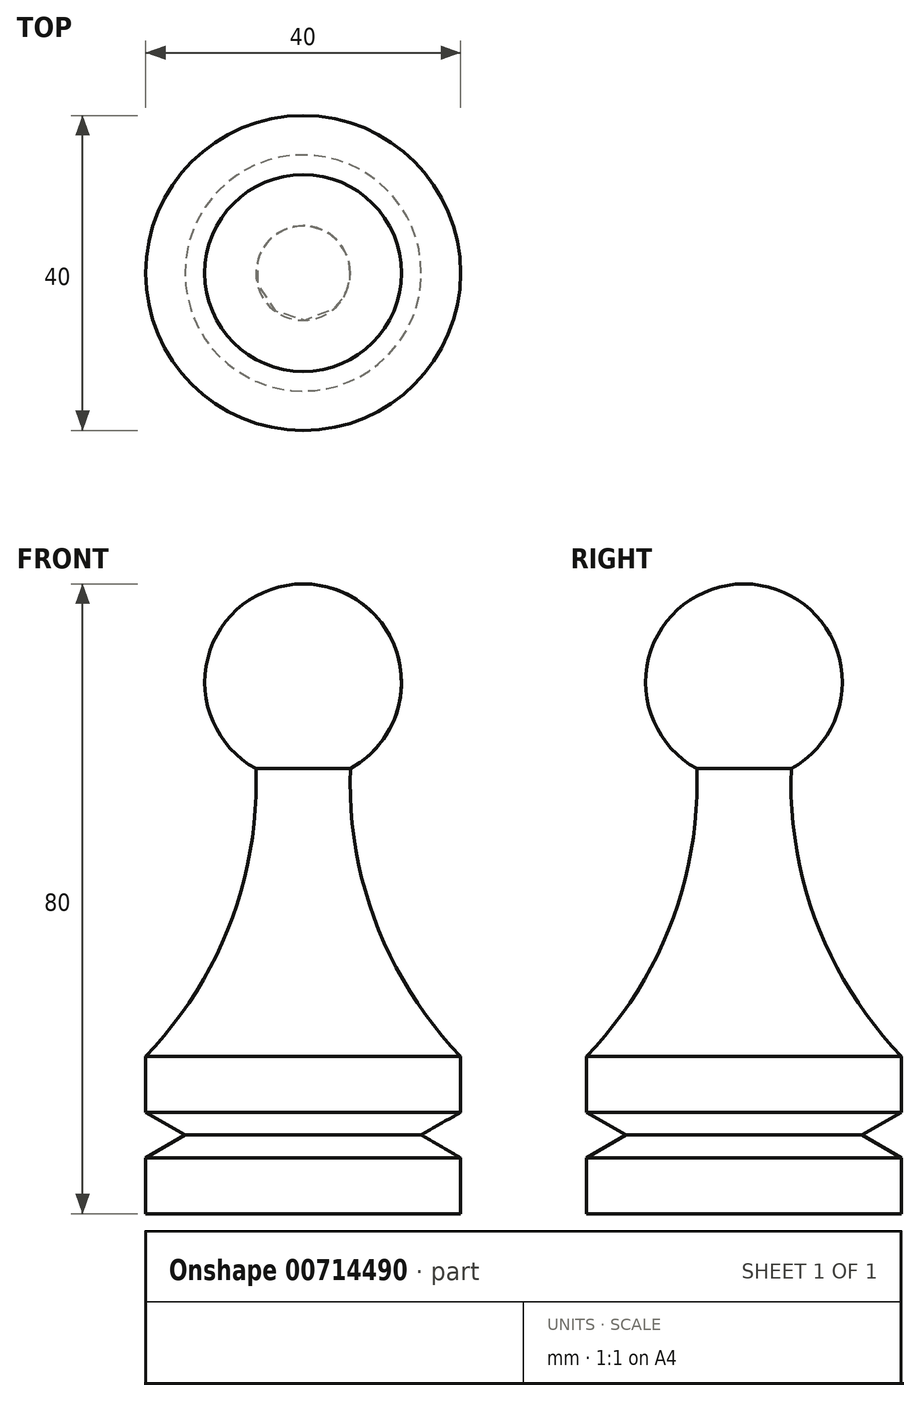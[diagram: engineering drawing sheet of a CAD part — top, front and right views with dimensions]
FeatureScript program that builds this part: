
annotation { "Feature Type Name" : "Feature", "Feature Type Description" : "" }
export const myFeature = defineFeature(function(context is Context, id is Id, definition is map)
    precondition{}
    {
        {
            var Q0;
            Q0=qCreatedBy(makeId("Front.planeOp"),FACE);
            var sketch = newSketch(context, id + "F0", { "sketchPlane" : qUnion([Q0])});
            skLineSegment(sketch, "E0", {"start": v(0, 99.5) * mm, "end": v(0, -75.6) * mm, "construction": true});
            skLineSegment(sketch, "E1", {"start": v(0, 0) * mm, "end": v(20, 0) * mm});
            skLineSegment(sketch, "E2", {"start": v(20, 0) * mm, "end": v(20, 7.11) * mm});
            skLineSegment(sketch, "E3", {"start": v(15, 10) * mm, "end": v(20, 7.11) * mm});
            skLineSegment(sketch, "E4", {"start": v(20, 12.89) * mm, "end": v(15, 10) * mm});
            skLineSegment(sketch, "E5", {"start": v(20, 12.89) * mm, "end": v(20, 20) * mm});
            skArc(sketch, "E6", {"start": v(6, 56.53) * mm, "mid": v(9.28, 36.84) * mm, "end": v(20, 20) * mm});
            skArc(sketch, "E7", {"start": v(6, 56.53) * mm, "mid": v(12.11, 70.6) * mm, "end": v(0, 80) * mm});
            skLineSegment(sketch, "E8", {"start": v(0, 80) * mm, "end": v(0, 0) * mm});
            skSolve(sketch);
        }
        {
            var Q0;
            Q0=makeQuery(id+"F0.imprint","IMPRINT",FACE,{"disambiguationData":[TD([[makeQuery(id+"F0.imprint","IMPRINT",EDGE,{"derivedFrom":sQuery(id+"F0.wireOp",EDGE,"E1")}),1.0]])]});
            var Q1;
            Q1=sQuery(id+"F0.wireOp",EDGE,"E8");
            revolve(context, id + "F1", {"surfaceOperationType" : NewSurfaceOperationType.NEW, "entities" : qUnion([Q0]), "axis" : qUnion([Q1]), "revolveType" : RevolveType.FULL});
        }
    });
